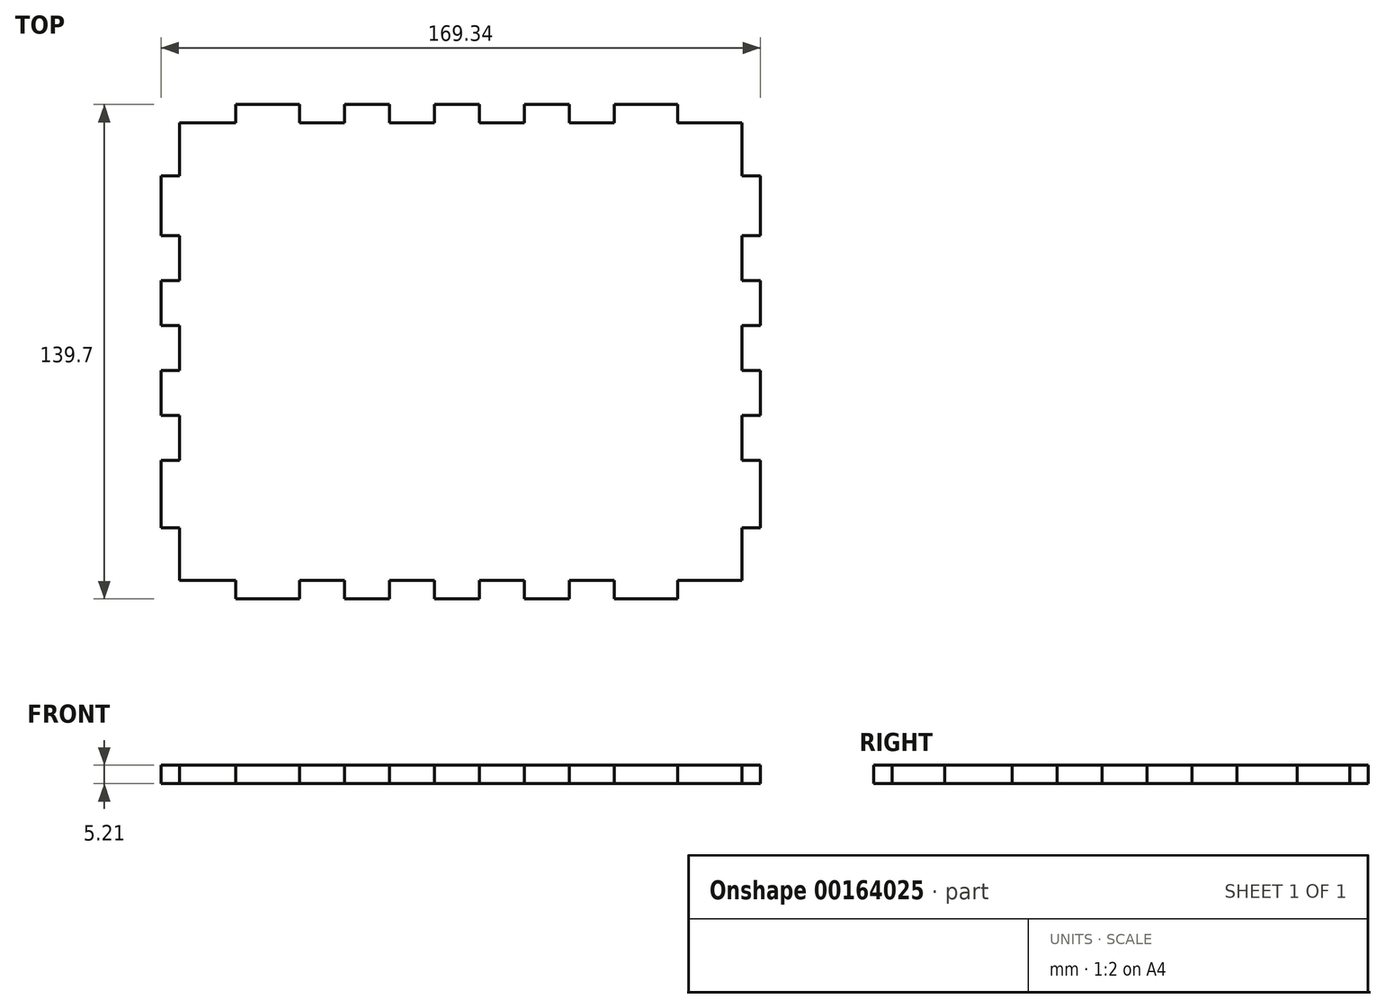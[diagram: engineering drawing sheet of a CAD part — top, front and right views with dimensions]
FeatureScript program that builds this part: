
annotation { "Feature Type Name" : "Feature", "Feature Type Description" : "" }
export const myFeature = defineFeature(function(context is Context, id is Id, definition is map)
    precondition{}
    {
        {
            var Q0;
            Q0=qCreatedBy(makeId("Top.planeOp"),FACE);
            var sketch = newSketch(context, id + "F0", { "sketchPlane" : qUnion([Q0])});
            skLineSegment(sketch, "E0.bottom", {"start": v(84.67, -69.85) * mm, "end": v(-84.67, -69.85) * mm});
            skLineSegment(sketch, "E0.top", {"start": v(84.67, 69.85) * mm, "end": v(-84.67, 69.85) * mm});
            skLineSegment(sketch, "E0.left", {"start": v(84.67, -69.85) * mm, "end": v(84.67, 69.85) * mm});
            skLineSegment(sketch, "E0.right", {"start": v(-84.67, -69.85) * mm, "end": v(-84.67, 69.85) * mm});
            skPoint(sketch, "E0.middle", {"position": v(0, 0) * mm});
            skSolve(sketch);
        }
        {
            var Q0;
            Q0=makeQuery(id+"F0.imprint","IMPRINT",FACE,{"disambiguationData":[TD([[makeQuery(id+"F0.imprint","IMPRINT",EDGE,{"derivedFrom":sQuery(id+"F0.wireOp",EDGE,"E0.bottom")}),-1.0]])]});
            extrude(context, id + "F1", {"entities" : qUnion([Q0]), "depth" : 5.2 * mm});
        }
        {
            var Q0;
            Q0=makeQuery(id+"F1.opExtrude","CAP_FACE",FACE,{"disambiguationData":[OSD([sQuery(id+"F0.wireOp",EDGE,"E0.bottom"),sQuery(id+"F0.wireOp",EDGE,"E0.top"),sQuery(id+"F0.wireOp",EDGE,"E0.left"),sQuery(id+"F0.wireOp",EDGE,"E0.right")])],"isStart":false});
            var sketch = newSketch(context, id + "F2", { "sketchPlane" : qUnion([Q0])});
            skLineSegment(sketch, "E1", {"start": v(-79.46, 64.64) * mm, "end": v(-79.46, 49.74) * mm});
            skLineSegment(sketch, "E2", {"start": v(-79.46, 49.74) * mm, "end": v(-84.67, 49.74) * mm});
            skLineSegment(sketch, "E3", {"start": v(-84.67, 49.74) * mm, "end": v(-84.67, 32.8) * mm});
            skLineSegment(sketch, "E4", {"start": v(-84.67, 32.8) * mm, "end": v(-79.46, 32.8) * mm});
            skLineSegment(sketch, "E5", {"start": v(-79.46, 32.8) * mm, "end": v(-79.46, 20.1) * mm});
            skLineSegment(sketch, "E6", {"start": v(-79.46, 20.1) * mm, "end": v(-84.67, 20.1) * mm});
            skLineSegment(sketch, "E7", {"start": v(-84.67, 20.1) * mm, "end": v(-84.67, 7.4) * mm});
            skLineSegment(sketch, "E8", {"start": v(-84.67, 7.4) * mm, "end": v(-79.46, 7.4) * mm});
            skLineSegment(sketch, "E9", {"start": v(-79.46, 7.4) * mm, "end": v(-79.46, -5.3) * mm});
            skLineSegment(sketch, "E10", {"start": v(-79.46, -5.3) * mm, "end": v(-84.67, -5.3) * mm});
            skLineSegment(sketch, "E11", {"start": v(-84.67, -5.3) * mm, "end": v(-84.67, -18) * mm});
            skLineSegment(sketch, "E12", {"start": v(-84.67, -18) * mm, "end": v(-79.46, -18) * mm});
            skLineSegment(sketch, "E13", {"start": v(-79.46, -18) * mm, "end": v(-79.46, -30.7) * mm});
            skLineSegment(sketch, "E14", {"start": v(-79.46, -30.7) * mm, "end": v(-84.67, -30.7) * mm});
            skLineSegment(sketch, "E15", {"start": v(-84.67, -30.7) * mm, "end": v(-84.67, -49.74) * mm});
            skLineSegment(sketch, "E16", {"start": v(-84.67, -49.74) * mm, "end": v(-79.46, -49.74) * mm});
            skLineSegment(sketch, "E17", {"start": v(-79.46, -49.74) * mm, "end": v(-79.46, -64.64) * mm});
            skLineSegment(sketch, "E18", {"start": v(-63.58, 69.85) * mm, "end": v(-45.49, 69.85) * mm});
            skLineSegment(sketch, "E19", {"start": v(-45.49, 69.85) * mm, "end": v(-45.49, 64.64) * mm});
            skLineSegment(sketch, "E20", {"start": v(-45.49, 64.64) * mm, "end": v(-32.79, 64.64) * mm});
            skLineSegment(sketch, "E21", {"start": v(-32.79, 64.64) * mm, "end": v(-32.79, 69.85) * mm});
            skLineSegment(sketch, "E22", {"start": v(-32.79, 69.85) * mm, "end": v(-20.09, 69.85) * mm});
            skLineSegment(sketch, "E23", {"start": v(-20.09, 69.85) * mm, "end": v(-20.09, 64.64) * mm});
            skLineSegment(sketch, "E24", {"start": v(-7.39, 69.85) * mm, "end": v(5.31, 69.85) * mm});
            skLineSegment(sketch, "E25", {"start": v(5.31, 69.85) * mm, "end": v(5.31, 64.64) * mm});
            skLineSegment(sketch, "E26", {"start": v(5.31, 64.64) * mm, "end": v(18.01, 64.64) * mm});
            skLineSegment(sketch, "E27", {"start": v(18.01, 64.64) * mm, "end": v(18.01, 69.85) * mm});
            skLineSegment(sketch, "E28", {"start": v(18.01, 69.85) * mm, "end": v(30.71, 69.85) * mm});
            skLineSegment(sketch, "E29", {"start": v(30.71, 69.85) * mm, "end": v(30.71, 64.64) * mm});
            skLineSegment(sketch, "E30", {"start": v(30.71, 64.64) * mm, "end": v(43.41, 64.64) * mm});
            skLineSegment(sketch, "E31", {"start": v(43.41, 64.64) * mm, "end": v(43.41, 69.85) * mm});
            skLineSegment(sketch, "E32", {"start": v(43.41, 69.85) * mm, "end": v(61.36, 69.85) * mm});
            skLineSegment(sketch, "E33", {"start": v(61.36, 69.85) * mm, "end": v(61.36, 64.64) * mm});
            skLineSegment(sketch, "E34", {"start": v(61.36, 64.64) * mm, "end": v(79.46, 64.64) * mm});
            skLineSegment(sketch, "E35", {"start": v(79.46, 49.74) * mm, "end": v(84.67, 49.74) * mm});
            skLineSegment(sketch, "E36", {"start": v(84.67, 49.74) * mm, "end": v(84.67, 32.8) * mm});
            skLineSegment(sketch, "E37", {"start": v(84.67, 32.8) * mm, "end": v(79.46, 32.8) * mm});
            skLineSegment(sketch, "E38", {"start": v(79.46, 32.8) * mm, "end": v(79.46, 20.1) * mm});
            skLineSegment(sketch, "E39", {"start": v(79.46, 20.1) * mm, "end": v(84.67, 20.1) * mm});
            skLineSegment(sketch, "E40", {"start": v(84.67, 20.1) * mm, "end": v(84.67, 7.4) * mm});
            skLineSegment(sketch, "E41", {"start": v(84.67, 7.4) * mm, "end": v(79.46, 7.4) * mm});
            skLineSegment(sketch, "E42", {"start": v(79.46, 7.4) * mm, "end": v(79.46, -5.3) * mm});
            skLineSegment(sketch, "E43", {"start": v(79.46, -5.3) * mm, "end": v(84.67, -5.3) * mm});
            skLineSegment(sketch, "E44", {"start": v(84.67, -5.3) * mm, "end": v(84.67, -18) * mm});
            skLineSegment(sketch, "E45", {"start": v(84.67, -18) * mm, "end": v(79.46, -18) * mm});
            skLineSegment(sketch, "E46", {"start": v(79.46, -18) * mm, "end": v(79.46, -30.7) * mm});
            skLineSegment(sketch, "E47", {"start": v(79.46, -30.7) * mm, "end": v(84.67, -30.7) * mm});
            skLineSegment(sketch, "E48", {"start": v(84.67, -30.7) * mm, "end": v(84.67, -49.74) * mm});
            skLineSegment(sketch, "E49", {"start": v(84.67, -49.74) * mm, "end": v(79.46, -49.74) * mm});
            skLineSegment(sketch, "E50", {"start": v(79.46, -49.74) * mm, "end": v(79.46, -64.64) * mm});
            skLineSegment(sketch, "E51", {"start": v(-79.46, -64.64) * mm, "end": v(-63.58, -64.64) * mm});
            skLineSegment(sketch, "E52", {"start": v(-63.58, -64.64) * mm, "end": v(-63.58, -69.85) * mm});
            skLineSegment(sketch, "E53", {"start": v(-63.58, -69.85) * mm, "end": v(-45.49, -69.85) * mm});
            skLineSegment(sketch, "E54", {"start": v(-45.49, -69.85) * mm, "end": v(-45.49, -64.64) * mm});
            skLineSegment(sketch, "E55", {"start": v(-45.49, -64.64) * mm, "end": v(-32.79, -64.64) * mm});
            skLineSegment(sketch, "E56", {"start": v(-32.79, -64.64) * mm, "end": v(-32.79, -69.85) * mm});
            skLineSegment(sketch, "E57", {"start": v(-32.79, -69.85) * mm, "end": v(-20.09, -69.85) * mm});
            skLineSegment(sketch, "E58", {"start": v(-20.09, -69.85) * mm, "end": v(-20.09, -64.64) * mm});
            skLineSegment(sketch, "E59", {"start": v(-20.09, -64.64) * mm, "end": v(-7.39, -64.64) * mm});
            skLineSegment(sketch, "E60", {"start": v(-7.39, -64.64) * mm, "end": v(-7.39, -69.85) * mm});
            skLineSegment(sketch, "E61", {"start": v(-7.39, -69.85) * mm, "end": v(5.31, -69.85) * mm});
            skLineSegment(sketch, "E62", {"start": v(5.31, -69.85) * mm, "end": v(5.31, -64.64) * mm});
            skLineSegment(sketch, "E63", {"start": v(43.41, -64.64) * mm, "end": v(43.41, -69.85) * mm});
            skLineSegment(sketch, "E64", {"start": v(43.41, -69.85) * mm, "end": v(61.36, -69.85) * mm});
            skLineSegment(sketch, "E65", {"start": v(61.36, -69.85) * mm, "end": v(61.36, -64.64) * mm});
            skLineSegment(sketch, "E66", {"start": v(61.36, -64.64) * mm, "end": v(79.46, -64.64) * mm});
            skLineSegment(sketch, "E67", {"start": v(-7.39, 69.85) * mm, "end": v(-7.39, 64.64) * mm});
            skLineSegment(sketch, "E68", {"start": v(-7.39, 64.64) * mm, "end": v(-20.09, 64.64) * mm});
            skLineSegment(sketch, "E69", {"start": v(43.41, -64.64) * mm, "end": v(30.71, -64.64) * mm});
            skLineSegment(sketch, "E70", {"start": v(30.71, -64.64) * mm, "end": v(30.71, -69.85) * mm});
            skLineSegment(sketch, "E71", {"start": v(18.01, -64.64) * mm, "end": v(5.31, -64.64) * mm});
            skLineSegment(sketch, "E72", {"start": v(-63.58, 69.85) * mm, "end": v(-63.58, 64.64) * mm});
            skLineSegment(sketch, "E73", {"start": v(-63.58, 64.64) * mm, "end": v(-79.46, 64.64) * mm});
            skLineSegment(sketch, "E74", {"start": v(79.46, 64.64) * mm, "end": v(79.46, 49.74) * mm});
            skLineSegment(sketch, "E75", {"start": v(18.01, -64.64) * mm, "end": v(18.01, -69.85) * mm});
            skLineSegment(sketch, "E76", {"start": v(18.01, -69.85) * mm, "end": v(30.71, -69.85) * mm});
            skSolve(sketch);
        }
        {
            var Q0;
            Q0=makeQuery(id+"F2.imprint","IMPRINT",FACE,{"disambiguationData":[TD([[makeQuery(id+"F2.imprint","IMPRINT",EDGE,{"derivedFrom":sQuery(id+"F2.wireOp",EDGE,"E1")}),-1.0]])]});
            var Q1;
            {var subQ0=sQuery(id+"F2.wireOp",EDGE,"E4");Q1=makeQuery(id+"F2.imprint","IMPRINT",FACE,{"disambiguationData":[TD([[makeQuery(id+"F2.imprint","IMPRINT",EDGE,{"derivedFrom":subQ0}),-1.0]])]});}
            var Q2;
            {var subQ0=sQuery(id+"F2.wireOp",EDGE,"E8");Q2=makeQuery(id+"F2.imprint","IMPRINT",FACE,{"disambiguationData":[TD([[makeQuery(id+"F2.imprint","IMPRINT",EDGE,{"derivedFrom":subQ0}),-1.0]])]});}
            var Q3;
            {var subQ0=sQuery(id+"F2.wireOp",EDGE,"E12");Q3=makeQuery(id+"F2.imprint","IMPRINT",FACE,{"disambiguationData":[TD([[makeQuery(id+"F2.imprint","IMPRINT",EDGE,{"derivedFrom":subQ0}),-1.0]])]});}
            var Q4;
            {var subQ1=sQuery(id+"F2.wireOp",EDGE,"E16");Q4=makeQuery(id+"F2.imprint","IMPRINT",FACE,{"disambiguationData":[TD([[makeQuery(id+"F2.imprint","IMPRINT",EDGE,{"derivedFrom":subQ1}),-1.0]])]});}
            var Q5;
            {var subQ0=sQuery(id+"F2.wireOp",EDGE,"E54");Q5=makeQuery(id+"F2.imprint","IMPRINT",FACE,{"disambiguationData":[TD([[makeQuery(id+"F2.imprint","IMPRINT",EDGE,{"derivedFrom":subQ0}),-1.0]])]});}
            var Q6;
            {var subQ0=sQuery(id+"F2.wireOp",EDGE,"E58");Q6=makeQuery(id+"F2.imprint","IMPRINT",FACE,{"disambiguationData":[TD([[makeQuery(id+"F2.imprint","IMPRINT",EDGE,{"derivedFrom":subQ0}),-1.0]])]});}
            var Q7;
            {var subQ0=sQuery(id+"F2.wireOp",EDGE,"E62");Q7=makeQuery(id+"F2.imprint","IMPRINT",FACE,{"disambiguationData":[TD([[makeQuery(id+"F2.imprint","IMPRINT",EDGE,{"derivedFrom":subQ0}),-1.0]])]});}
            var Q8;
            {var subQ0=sQuery(id+"F2.wireOp",EDGE,"E63");Q8=makeQuery(id+"F2.imprint","IMPRINT",FACE,{"disambiguationData":[TD([[makeQuery(id+"F2.imprint","IMPRINT",EDGE,{"derivedFrom":subQ0}),-1.0]])]});}
            var Q9;
            {var subQ4=sQuery(id+"F2.wireOp",EDGE,"E49");Q9=makeQuery(id+"F2.imprint","IMPRINT",FACE,{"disambiguationData":[TD([[makeQuery(id+"F2.imprint","IMPRINT",EDGE,{"derivedFrom":subQ4}),1.0]])]});}
            var Q10;
            {var subQ0=sQuery(id+"F2.wireOp",EDGE,"E45");Q10=makeQuery(id+"F2.imprint","IMPRINT",FACE,{"disambiguationData":[TD([[makeQuery(id+"F2.imprint","IMPRINT",EDGE,{"derivedFrom":subQ0}),1.0]])]});}
            var Q11;
            {var subQ0=sQuery(id+"F2.wireOp",EDGE,"E41");Q11=makeQuery(id+"F2.imprint","IMPRINT",FACE,{"disambiguationData":[TD([[makeQuery(id+"F2.imprint","IMPRINT",EDGE,{"derivedFrom":subQ0}),1.0]])]});}
            var Q12;
            {var subQ1=sQuery(id+"F2.wireOp",EDGE,"E33");Q12=makeQuery(id+"F2.imprint","IMPRINT",FACE,{"disambiguationData":[TD([[makeQuery(id+"F2.imprint","IMPRINT",EDGE,{"derivedFrom":subQ1}),1.0]])]});}
            var Q13;
            {var subQ0=sQuery(id+"F2.wireOp",EDGE,"E29");Q13=makeQuery(id+"F2.imprint","IMPRINT",FACE,{"disambiguationData":[TD([[makeQuery(id+"F2.imprint","IMPRINT",EDGE,{"derivedFrom":subQ0}),1.0]])]});}
            var Q14;
            {var subQ0=sQuery(id+"F2.wireOp",EDGE,"E25");Q14=makeQuery(id+"F2.imprint","IMPRINT",FACE,{"disambiguationData":[TD([[makeQuery(id+"F2.imprint","IMPRINT",EDGE,{"derivedFrom":subQ0}),1.0]])]});}
            var Q15;
            {var subQ0=sQuery(id+"F2.wireOp",EDGE,"E37");Q15=makeQuery(id+"F2.imprint","IMPRINT",FACE,{"disambiguationData":[TD([[makeQuery(id+"F2.imprint","IMPRINT",EDGE,{"derivedFrom":subQ0}),1.0]])]});}
            var Q16;
            {var subQ0=sQuery(id+"F2.wireOp",EDGE,"E23");Q16=makeQuery(id+"F2.imprint","IMPRINT",FACE,{"disambiguationData":[TD([[makeQuery(id+"F2.imprint","IMPRINT",EDGE,{"derivedFrom":subQ0}),1.0]])]});}
            var Q17;
            {var subQ0=sQuery(id+"F2.wireOp",EDGE,"E19");Q17=makeQuery(id+"F2.imprint","IMPRINT",FACE,{"disambiguationData":[TD([[makeQuery(id+"F2.imprint","IMPRINT",EDGE,{"derivedFrom":subQ0}),1.0]])]});}
            extrude(context, id + "F3", {"entities" : qUnion([Q0, Q1, Q2, Q3, Q4, Q5, Q6, Q7, Q8, Q9, Q10, Q11, Q12, Q13, Q14, Q15, Q16, Q17]), "operationType" : NewBodyOperationType.REMOVE, "endBound" : BoundingType.THROUGH_ALL, "oppositeDirection" : true, "depth" : 25.4 * mm});
        }
    });
